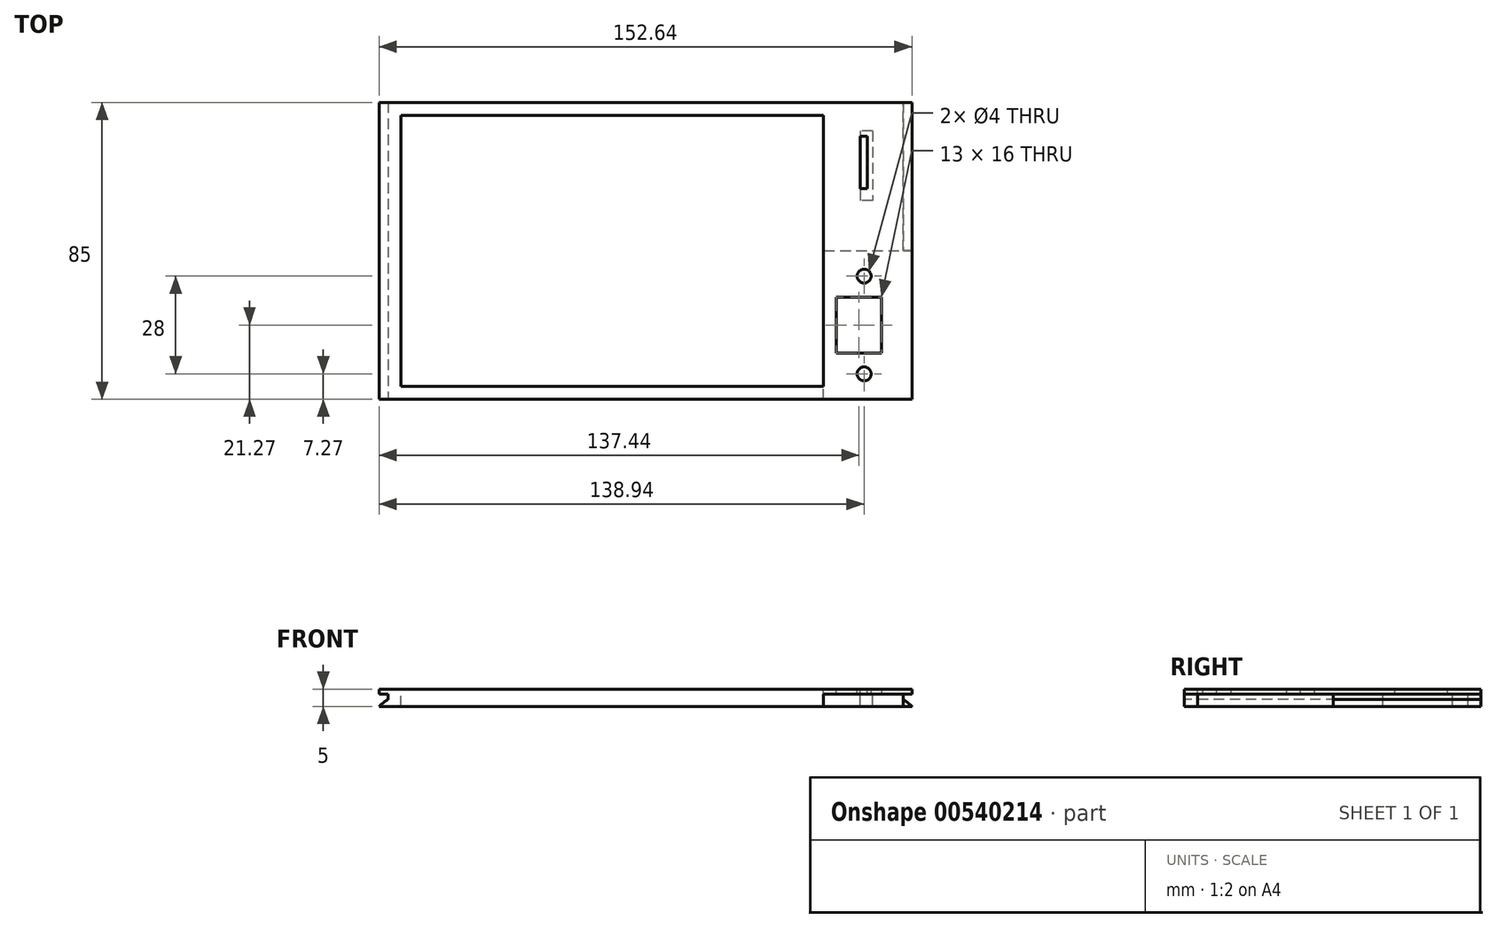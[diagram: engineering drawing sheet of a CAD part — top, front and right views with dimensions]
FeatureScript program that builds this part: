
annotation { "Feature Type Name" : "Feature", "Feature Type Description" : "" }
export const myFeature = defineFeature(function(context is Context, id is Id, definition is map)
    precondition{}
    {
        {
            var Q0;
            Q0=qCreatedBy(makeId("Top.planeOp"),FACE);
            var sketch = newSketch(context, id + "F0", { "sketchPlane" : qUnion([Q0])});
            skLineSegment(sketch, "E0.bottom", {"start": v(-73.82, 43.73) * mm, "end": v(73.82, 43.73) * mm});
            skLineSegment(sketch, "E0.top", {"start": v(-73.82, -41.27) * mm, "end": v(73.82, -41.27) * mm});
            skLineSegment(sketch, "E0.left", {"start": v(-73.82, 43.73) * mm, "end": v(-73.82, -41.27) * mm});
            skLineSegment(sketch, "E0.right", {"start": v(73.82, 43.73) * mm, "end": v(73.82, -41.27) * mm});
            skLineSegment(sketch, "E1", {"start": v(-85.87, 1.23) * mm, "end": v(82.85, 1.23) * mm, "construction": true});
            skPoint(sketch, "E1.startSnap0", {"position": v(-73.82, 1.23) * mm});
            skLineSegment(sketch, "E2", {"start": v(0, 48.2) * mm, "end": v(0, -46) * mm, "construction": true});
            skPoint(sketch, "E2.startSnap0", {"position": v(0, 43.73) * mm});
            skPoint(sketch, "E2.endSnap0", {"position": v(0, -41.27) * mm});
            skLineSegment(sketch, "E3.bottom", {"start": v(-70.07, 39.98) * mm, "end": v(50.93, 39.98) * mm});
            skLineSegment(sketch, "E3.top", {"start": v(-70.07, -37.52) * mm, "end": v(50.93, -37.52) * mm});
            skLineSegment(sketch, "E3.left", {"start": v(-70.07, 39.98) * mm, "end": v(-70.07, -37.52) * mm});
            skLineSegment(sketch, "E3.right", {"start": v(50.93, 39.98) * mm, "end": v(50.93, -37.52) * mm});
            skLineSegment(sketch, "E4.bottom", {"start": v(67.62, -28) * mm, "end": v(54.62, -28) * mm});
            skLineSegment(sketch, "E4.top", {"start": v(67.62, -12) * mm, "end": v(54.62, -12) * mm});
            skLineSegment(sketch, "E4.left", {"start": v(67.62, -28) * mm, "end": v(67.62, -12) * mm});
            skLineSegment(sketch, "E4.right", {"start": v(54.62, -28) * mm, "end": v(54.62, -12) * mm});
            skCircle(sketch, "E5", {"center": v(62.62, -34) * mm, "radius": 2 * mm});
            skCircle(sketch, "E6.MirrorC", {"center": v(62.62, -6) * mm, "radius": 2 * mm});
            skLineSegment(sketch, "E7.bottom", {"start": v(61.5, 34.09) * mm, "end": v(63.5, 34.09) * mm});
            skLineSegment(sketch, "E7.top", {"start": v(61.5, 19.09) * mm, "end": v(63.5, 19.09) * mm});
            skLineSegment(sketch, "E7.left", {"start": v(61.5, 34.09) * mm, "end": v(61.5, 19.09) * mm});
            skLineSegment(sketch, "E7.right", {"start": v(63.5, 34.09) * mm, "end": v(63.5, 19.09) * mm});
            skSolve(sketch);
        }
        {
            var Q0;
            Q0 = qSketchRegion(id + "F0", true);
            extrude(context, id + "F1", {"entities" : qUnion([Q0]), "oppositeDirection" : true, "depth" : 5 * mm, "offsetDistance" : 25 * mm});
        }
        {
            var Q0;
            Q0=qCreatedBy(makeId("Top.planeOp"),FACE);
            var sketch = newSketch(context, id + "F2", { "sketchPlane" : qUnion([Q0])});
            skLineSegment(sketch, "E8.bottom", {"start": v(-76.32, 43.73) * mm, "end": v(-73.82, 43.73) * mm});
            skLineSegment(sketch, "E8.top", {"start": v(-76.32, -41.27) * mm, "end": v(-73.82, -41.27) * mm});
            skLineSegment(sketch, "E8.left", {"start": v(-76.32, 43.73) * mm, "end": v(-76.32, -41.27) * mm});
            skLineSegment(sketch, "E8.right", {"start": v(-73.82, 43.73) * mm, "end": v(-73.82, -41.27) * mm});
            skLineSegment(sketch, "E9.bottom", {"start": v(73.82, 43.73) * mm, "end": v(76.32, 43.73) * mm});
            skLineSegment(sketch, "E9.top", {"start": v(73.82, -41.27) * mm, "end": v(76.32, -41.27) * mm});
            skLineSegment(sketch, "E9.left", {"start": v(73.82, 43.73) * mm, "end": v(73.82, -41.27) * mm});
            skLineSegment(sketch, "E9.right", {"start": v(76.32, 43.73) * mm, "end": v(76.32, -41.27) * mm});
            skSolve(sketch);
        }
        {
            var Q0;
            Q0=makeQuery(id+"F2.imprint","IMPRINT",FACE,{"disambiguationData":[TD([[makeQuery(id+"F2.imprint","IMPRINT",EDGE,{"derivedFrom":sQuery(id+"F2.wireOp",EDGE,"E8.bottom")}),-1.0]])]});
            var Q1;
            Q1=makeQuery(id+"F2.imprint","IMPRINT",FACE,{"disambiguationData":[TD([[makeQuery(id+"F2.imprint","IMPRINT",EDGE,{"derivedFrom":sQuery(id+"F2.wireOp",EDGE,"E9.bottom")}),-1.0]])]});
            extrude(context, id + "F3", {"entities" : qUnion([Q0, Q1]), "operationType" : NewBodyOperationType.ADD, "oppositeDirection" : true, "depth" : 1.5 * mm, "offsetDistance" : 25 * mm, "hasSecondDirection" : true, "secondDirectionOppositeDirection" : true, "secondDirectionDepth" : 0 * mm});
        }
        {
            var Q0;
            Q0=qCreatedBy(makeId("Top.planeOp"),FACE);
            var sketch = newSketch(context, id + "F4", { "sketchPlane" : qUnion([Q0])});
            skLineSegment(sketch, "E10.bottom", {"start": v(51.18, -41.27) * mm, "end": v(73.82, -41.27) * mm});
            skLineSegment(sketch, "E10.top", {"start": v(51.18, 1.33) * mm, "end": v(73.82, 1.33) * mm});
            skLineSegment(sketch, "E10.left", {"start": v(50.93, -41.27) * mm, "end": v(50.93, 1.33) * mm});
            skLineSegment(sketch, "E10.right", {"start": v(73.82, -41.27) * mm, "end": v(73.82, 1.33) * mm});
            skLineSegment(sketch, "E11.bottom", {"start": v(67.62, -28) * mm, "end": v(54.62, -28) * mm});
            skLineSegment(sketch, "E11.top", {"start": v(67.62, -12) * mm, "end": v(54.62, -12) * mm});
            skLineSegment(sketch, "E11.left", {"start": v(67.62, -28) * mm, "end": v(67.62, -12) * mm});
            skLineSegment(sketch, "E11.right", {"start": v(54.62, -28) * mm, "end": v(54.62, -12) * mm});
            skCircle(sketch, "E12", {"center": v(62.62, -34) * mm, "radius": 2 * mm});
            skCircle(sketch, "E13.MirrorC", {"center": v(62.62, -6) * mm, "radius": 2 * mm});
            skLineSegment(sketch, "E14", {"start": v(50.93, -41.27) * mm, "end": v(51.18, -41.27) * mm});
            skLineSegment(sketch, "E15", {"start": v(50.93, 1.33) * mm, "end": v(51.18, 1.33) * mm});
            skSolve(sketch);
        }
        {
            var Q0;
            Q0 = qSketchRegion(id + "F4", true);
            extrude(context, id + "F5", {"entities" : qUnion([Q0]), "operationType" : NewBodyOperationType.REMOVE, "oppositeDirection" : true, "depth" : 5 * mm, "offsetDistance" : 25 * mm, "hasSecondDirection" : true, "secondDirectionOppositeDirection" : true, "secondDirectionDepth" : 1.5 * mm});
        }
        {
            var Q0;
            Q0=qCreatedBy(makeId("Top.planeOp"),FACE);
            var sketch = newSketch(context, id + "F6", { "sketchPlane" : qUnion([Q0])});
            skLineSegment(sketch, "E16.bottom", {"start": v(65, 35.59) * mm, "end": v(61.5, 35.59) * mm});
            skLineSegment(sketch, "E16.top", {"start": v(65, 15.59) * mm, "end": v(61.5, 15.59) * mm});
            skLineSegment(sketch, "E16.left", {"start": v(65, 35.59) * mm, "end": v(65, 15.59) * mm});
            skLineSegment(sketch, "E16.right", {"start": v(61.5, 35.59) * mm, "end": v(61.5, 15.59) * mm});
            skSolve(sketch);
        }
        {
            var Q0;
            Q0 = qSketchRegion(id + "F6", true);
            extrude(context, id + "F7", {"entities" : qUnion([Q0]), "operationType" : NewBodyOperationType.REMOVE, "oppositeDirection" : true, "depth" : 5 * mm, "offsetDistance" : 25 * mm, "hasSecondDirection" : true, "secondDirectionOppositeDirection" : true, "secondDirectionDepth" : 1.5 * mm});
        }
        {
            var Q0;
            Q0=qCreatedBy(makeId("Top.planeOp"),FACE);
            var sketch = newSketch(context, id + "F8", { "sketchPlane" : qUnion([Q0])});
            skLineSegment(sketch, "E17.bottom", {"start": v(-76.32, 43.73) * mm, "end": v(-73.82, 43.73) * mm});
            skLineSegment(sketch, "E17.top", {"start": v(-76.32, -41.27) * mm, "end": v(-73.82, -41.27) * mm});
            skLineSegment(sketch, "E17.left", {"start": v(-76.32, 43.73) * mm, "end": v(-76.32, -41.27) * mm});
            skLineSegment(sketch, "E17.right", {"start": v(-73.82, 43.73) * mm, "end": v(-73.82, -41.27) * mm});
            skLineSegment(sketch, "E18.bottom", {"start": v(73.82, 43.73) * mm, "end": v(76.32, 43.73) * mm});
            skLineSegment(sketch, "E18.left", {"start": v(73.82, 43.73) * mm, "end": v(73.82, 1.33) * mm});
            skLineSegment(sketch, "E18.right", {"start": v(76.32, 43.73) * mm, "end": v(76.32, 1.33) * mm});
            skLineSegment(sketch, "E19", {"start": v(73.82, 1.33) * mm, "end": v(76.32, 1.33) * mm});
            skSolve(sketch);
        }
        {
            var Q0;
            Q0 = qSketchRegion(id + "F8", true);
            extrude(context, id + "F9", {"entities" : qUnion([Q0]), "operationType" : NewBodyOperationType.ADD, "oppositeDirection" : true, "depth" : 5 * mm, "offsetDistance" : 25 * mm, "hasSecondDirection" : true, "secondDirectionOppositeDirection" : true, "secondDirectionDepth" : 3 * mm});
        }
        {
            var Q0;
            Q0=makeQuery(id+"F9.opExtrude","CAP_EDGE",EDGE,{"disambiguationData":[OSD([sQuery(id+"F8.wireOp",EDGE,"E17.left")])],"isStart":true});
            fillet(context, id + "F10", {"entities" : qUnion([Q0]), "radius" : 3 * mm, "tangentPropagation" : true, "rho" : 0.1, "crossSection" : FilletCrossSection.CONIC, "allowEdgeOverflow" : false});
        }
        {
            var Q0;
            Q0=makeQuery(id+"F9.opExtrude","CAP_EDGE",EDGE,{"disambiguationData":[OSD([sQuery(id+"F8.wireOp",EDGE,"E18.right")])],"isStart":true});
            fillet(context, id + "F11", {"entities" : qUnion([Q0]), "radius" : 3 * mm, "tangentPropagation" : true, "rho" : 0.1, "crossSection" : FilletCrossSection.CONIC, "allowEdgeOverflow" : false});
        }
    });
